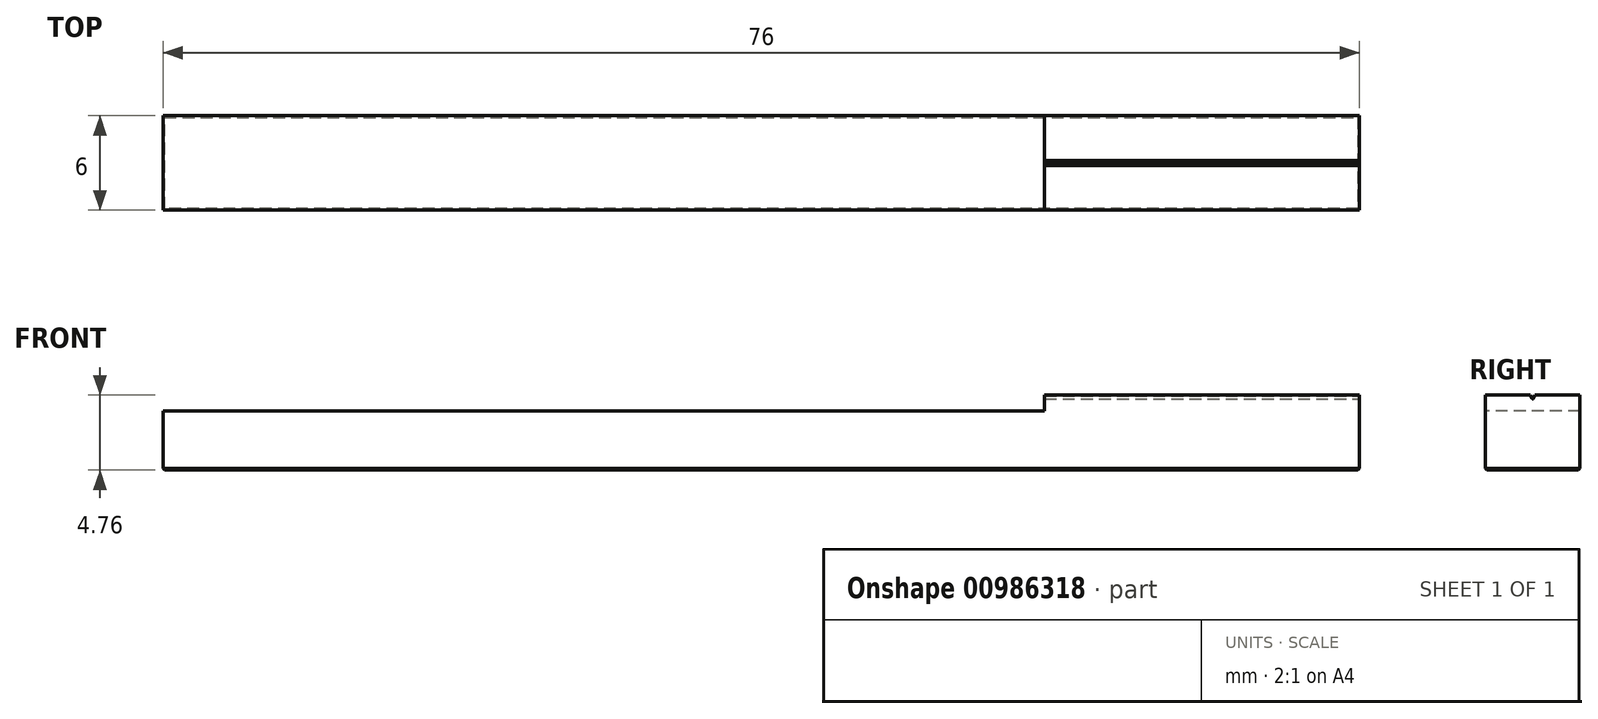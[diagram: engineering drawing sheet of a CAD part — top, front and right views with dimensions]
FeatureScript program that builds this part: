
annotation { "Feature Type Name" : "Feature", "Feature Type Description" : "" }
export const myFeature = defineFeature(function(context is Context, id is Id, definition is map)
    precondition{}
    {
        {
            var Q0;
            Q0=qCreatedBy(makeId("Top.planeOp"),FACE);
            var sketch = newSketch(context, id + "F0", { "sketchPlane" : qUnion([Q0])});
            skLineSegment(sketch, "E0.bottom", {"start": v(-38, 3) * mm, "end": v(38, 3) * mm});
            skLineSegment(sketch, "E0.top", {"start": v(-38, -3) * mm, "end": v(38, -3) * mm});
            skLineSegment(sketch, "E0.left", {"start": v(-38, 3) * mm, "end": v(-38, -3) * mm});
            skLineSegment(sketch, "E0.right", {"start": v(38, 3) * mm, "end": v(38, -3) * mm});
            skLineSegment(sketch, "E1", {"start": v(0, 9.05) * mm, "end": v(0, -9.2) * mm, "construction": true});
            skLineSegment(sketch, "E2", {"start": v(-9.84, 0) * mm, "end": v(11.26, 0) * mm, "construction": true});
            skSolve(sketch);
        }
        {
            var Q0;
            Q0=qSketchRegion(id+"F0",true);
            extrude(context, id + "F1", {"entities" : qUnion([Q0]), "depth" : 7 * mm, "offsetDistance" : 25 * mm});
        }
        {
            var Q0;
            Q0=makeQuery(id+"F1.opExtrude","CAP_FACE",FACE,{"disambiguationData":[OSD([sQuery(id+"F0.wireOp",EDGE,"E0.bottom"),sQuery(id+"F0.wireOp",EDGE,"E0.top"),sQuery(id+"F0.wireOp",EDGE,"E0.left"),sQuery(id+"F0.wireOp",EDGE,"E0.right")])],"isStart":false});
            var sketch = newSketch(context, id + "F2", { "sketchPlane" : qUnion([Q0])});
            skLineSegment(sketch, "E3.bottom", {"start": v(-38, -3) * mm, "end": v(38.92, -3) * mm});
            skLineSegment(sketch, "E3.top", {"start": v(-38, 3) * mm, "end": v(38.92, 3) * mm});
            skLineSegment(sketch, "E3.left", {"start": v(-38, -3) * mm, "end": v(-38, 3) * mm});
            skLineSegment(sketch, "E3.right", {"start": v(38.92, -3) * mm, "end": v(38.92, 3) * mm});
            skSolve(sketch);
        }
        {
            var Q0;
            Q0=qSketchRegion(id+"F2",true);
            extrude(context, id + "F3", {"entities" : qUnion([Q0]), "operationType" : NewBodyOperationType.REMOVE, "oppositeDirection" : true, "depth" : (7 - 4.76) * mm, "offsetDistance" : 25 * mm});
        }
        {
            var Q0;
            Q0=makeQuery(id+"F1.opExtrude","SWEPT_FACE",FACE,{"disambiguationData":[OSD([sQuery(id+"F0.wireOp",EDGE,"E0.right")])]});
            var sketch = newSketch(context, id + "F4", { "sketchPlane" : qUnion([Q0])});
            skLineSegment(sketch, "E4", {"start": v(-1.44, 7) * mm, "end": v(-0.1, 4.7) * mm});
            skLineSegment(sketch, "E5", {"start": v(1.44, 7) * mm, "end": v(-1.44, 7) * mm});
            skArc(sketch, "E6", {"start": v(-0.05, 4.55) * mm, "mid": v(0, 4.52) * mm, "end": v(0.05, 4.55) * mm});
            skLineSegment(sketch, "E7", {"start": v(-0.1, 4.7) * mm, "end": v(-0.05, 4.55) * mm});
            skLineSegment(sketch, "E8", {"start": v(0.05, 4.55) * mm, "end": v(0.1, 4.7) * mm});
            skLineSegment(sketch, "E9.trimOffspring", {"start": v(0.1, 4.7) * mm, "end": v(1.44, 7) * mm});
            skLineSegment(sketch, "E10", {"start": v(0, 7) * mm, "end": v(0, -0.68) * mm, "construction": true});
            skLineSegment(sketch, "E11", {"start": v(-0.05, 4.55) * mm, "end": v(0, 4.44) * mm, "construction": true});
            skLineSegment(sketch, "E12", {"start": v(0, 4.44) * mm, "end": v(0.05, 4.55) * mm, "construction": true});
            skSolve(sketch);
        }
        {
            var Q0;
            Q0=qSketchRegion(id+"F4",true);
            extrude(context, id + "F5", {"entities" : qUnion([Q0]), "operationType" : NewBodyOperationType.REMOVE, "endBound" : BoundingType.THROUGH_ALL, "oppositeDirection" : true, "depth" : 25 * mm, "offsetDistance" : 25 * mm});
        }
        {
            var Q0;
            Q0=makeQuery(id+"F1.opExtrude","CAP_EDGE",EDGE,{"disambiguationData":[OSD([sQuery(id+"F0.wireOp",EDGE,"E0.top")])],"isStart":true});
            var Q1;
            Q1=makeQuery(id+"F1.opExtrude","CAP_EDGE",EDGE,{"disambiguationData":[OSD([sQuery(id+"F0.wireOp",EDGE,"E0.right")])],"isStart":true});
            var Q2;
            Q2=makeQuery(id+"F1.opExtrude","CAP_EDGE",EDGE,{"disambiguationData":[OSD([sQuery(id+"F0.wireOp",EDGE,"E0.bottom")])],"isStart":true});
            var Q3;
            Q3=makeQuery(id+"F1.opExtrude","CAP_EDGE",EDGE,{"disambiguationData":[OSD([sQuery(id+"F0.wireOp",EDGE,"E0.left")])],"isStart":true});
            var Q4;
            {var subQ0=sQuery(id+"F2.wireOp",EDGE,"E3.left");Q4=makeQuery(id+"F5.boolean.opBoolean","SPLIT",EDGE,{"disambiguationData":[TD([makeQuery(id+"F1.opExtrude","SWEPT_FACE",FACE,{"disambiguationData":[OSD([sQuery(id+"F0.wireOp",EDGE,"E0.top")])]})])],"derivedFrom":makeQuery(id+"F3.boolean.opBoolean","COPY",EDGE,{"derivedFrom":makeQuery(id+"F3.opExtrude","CAP_EDGE",EDGE,{"disambiguationData":[OSD([subQ0])],"isStart":false})})});}
            var Q5;
            {var subQ0=sQuery(id+"F2.wireOp",EDGE,"E3.left");Q5=makeQuery(id+"F5.boolean.opBoolean","SPLIT",EDGE,{"disambiguationData":[TD([makeQuery(id+"F1.opExtrude","SWEPT_FACE",FACE,{"disambiguationData":[OSD([sQuery(id+"F0.wireOp",EDGE,"E0.bottom")])]})])],"derivedFrom":makeQuery(id+"F3.boolean.opBoolean","COPY",EDGE,{"derivedFrom":makeQuery(id+"F3.opExtrude","CAP_EDGE",EDGE,{"disambiguationData":[OSD([subQ0])],"isStart":false})})});}
            chamfer(context, id + "F6", {"entities" : qUnion([Q0, Q1, Q2, Q3, Q4, Q5]), "width" : 0.1 * mm, "tangentPropagation" : true});
        }
        {
            var Q0;
            Q0=makeQuery(id+"F5.boolean.opBoolean","SPLIT",FACE,{"disambiguationData":[TD([makeQuery(id+"F1.opExtrude","SWEPT_FACE",FACE,{"disambiguationData":[OSD([sQuery(id+"F0.wireOp",EDGE,"E0.bottom")])]})])],"derivedFrom":makeQuery(id+"F3.boolean.opBoolean","COPY",FACE,{"derivedFrom":makeQuery(id+"F3.opExtrude","CAP_FACE",FACE,{"disambiguationData":[OSD([sQuery(id+"F2.wireOp",EDGE,"E3.bottom"),sQuery(id+"F2.wireOp",EDGE,"E3.top"),sQuery(id+"F2.wireOp",EDGE,"E3.left"),sQuery(id+"F2.wireOp",EDGE,"E3.right")])],"isStart":false})})});
            var sketch = newSketch(context, id + "F7", { "sketchPlane" : qUnion([Q0])});
            skLineSegment(sketch, "E13.bottom", {"start": v(-40.95, 3) * mm, "end": v(18, 3) * mm});
            skLineSegment(sketch, "E13.top", {"start": v(-40.95, -3) * mm, "end": v(18, -3) * mm});
            skLineSegment(sketch, "E13.left", {"start": v(-40.95, 3) * mm, "end": v(-40.95, -3) * mm});
            skLineSegment(sketch, "E13.right", {"start": v(18, 3) * mm, "end": v(18, -3) * mm});
            skSolve(sketch);
        }
        {
            var Q0;
            Q0 = qSketchRegion(id + "F7", true);
            extrude(context, id + "F8", {"entities" : qUnion([Q0]), "operationType" : NewBodyOperationType.REMOVE, "oppositeDirection" : true, "depth" : 1 * mm, "offsetDistance" : 25 * mm});
        }
    });
